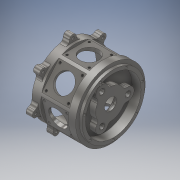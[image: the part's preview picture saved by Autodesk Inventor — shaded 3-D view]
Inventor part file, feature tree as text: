
AUTODESK INVENTOR PART (.ipt)
format: ipt  version: 2018 (Build 220112000, 112)  size: 587,776 bytes
history: native  units: mm
features: sketch x10, extrude x10, hole x4, pattern_circular x2, direct_edit x1, chamfer x1, other x1, revolve x1, projected_geometry x1
ambient origin geometry x8: Origin, YZ Plane, XZ Plane, XY Plane, X Axis, Y Axis, Z Axis, Center Point
bodies: Solid1 (feature_tree)
feature tree (31):
  sketch  "Sketch1"  dims[d0=100.0mm d1=90.0mm]
  extrude  "Extrusion1"  Depth=90.0mm
  extrude  "Extrusion2"  Depth=67.0mm TaperAngle=0.0deg
  extrude  "Extrusion3"  Depth=4.07mm
  extrude  "Extrusion4"  Depth=13.0mm TaperAngle=0.0deg
  extrude  "Extrusion5"  Depth=18.0mm
  direct_edit  "Direct Edit1"
  extrude  "Extrusion6"  Depth=12.0mm
  extrude  "Extrusion7"  Depth=30.0mm TaperAngle=360.0deg
  chamfer  "Chamfer1"  Distance=9.0mm
  extrude  "Extrusion8"  Depth=5.0mm
  sketch  "Sketch8"  dims[d28=8.0mm d29=30.0mm d31=360.0deg]
  extrude  "Extrusion9"  Depth=10.0mm TaperAngle=0.0deg
  hole  "Hole1"  [1 undecoded]
  extrude  "Extrusion10"  Depth=5.0mm TaperAngle=0.0deg
  hole  "Hole2"  [1 undecoded]
  hole  "Hole3"  [1 undecoded]
  other  "Work Axis1"
  pattern_circular  "Circular Pattern1"  [2 undecoded]
  hole  "Hole4"  [1 undecoded]
  pattern_circular  "Circular Pattern2"  [2 undecoded]
  sketch  "Sketch2"  dims[d2=80.0mm d3=67.0mm d4=0.0mm]
  sketch  "Sketch4"  dims[d5=4.07mm d6=0.0mm d7=85.0mm]
  sketch  "Sketch5"  dims[d8=50.0mm d9=0.0mm d10=13.0mm d11=0.0mm]
  sketch  "Sketch6"  dims[d12=43.0mm d22=21.5mm d25=18.0mm]
  sketch  "Sketch7"  dims[d26=25.0mm d27=12.0mm]
  sketch  "Sketch9"  dims[d33=21.5mm]
  sketch  "Sketch10"  dims[d34=21.5mm d35=9.0mm d36=0.0mm]
  sketch  "Sketch11"  dims[d37=-15.707963mm d38=35.0mm d39=10.0mm d40=0.0mm d41=17.35mm d42=17.0mm d43=0.0mm d44=2.0mm d45=2.0mm d46=45.0deg d47=40.0mm d48=10.43mm d49=46.0mm d50=39.19mm d51=0.0mm d53=39.19mm d54=0.0mm d55=27.0mm d57=19.595mm d58=32.0mm d59=32.0mm d60=3.242mm d61=8.0mm d62=3.023mm d63=2.0mm d64=14.3117mm d65=11.8mm d66=20.594885mm d67=20.0mm d69=13.0mm d70=9.0mm d71=0.0mm d72=10.0mm d73=10.0mm d74=4.134mm d75=10.0mm d76=3.023mm d77=2.0mm d78=14.3117mm d79=14.2mm d80=20.594885mm d81=46.0mm d82=3.242mm d83=8.0mm d84=3.023mm d85=2.0mm d86=14.3117mm d87=10.8mm d88=20.594885mm d89=70.0mm d90=360.0deg d92=85.0mm d93=3.242mm d94=8.0mm d95=3.023mm d96=2.0mm d97=14.3117mm d98=13.3mm d99=20.594885mm d100=70.0mm d101=360.0deg d103=55.0mm d104=5.0mm]
  revolve  "Rotate1"  [1 undecoded]
  projected_geometry  "Project Cut Edges1"
note: 9 required parameter values undecoded (feature->parameter linkage not recoverable at this tier; creation-order binding heuristic only, values carry confidence <= 0.55)